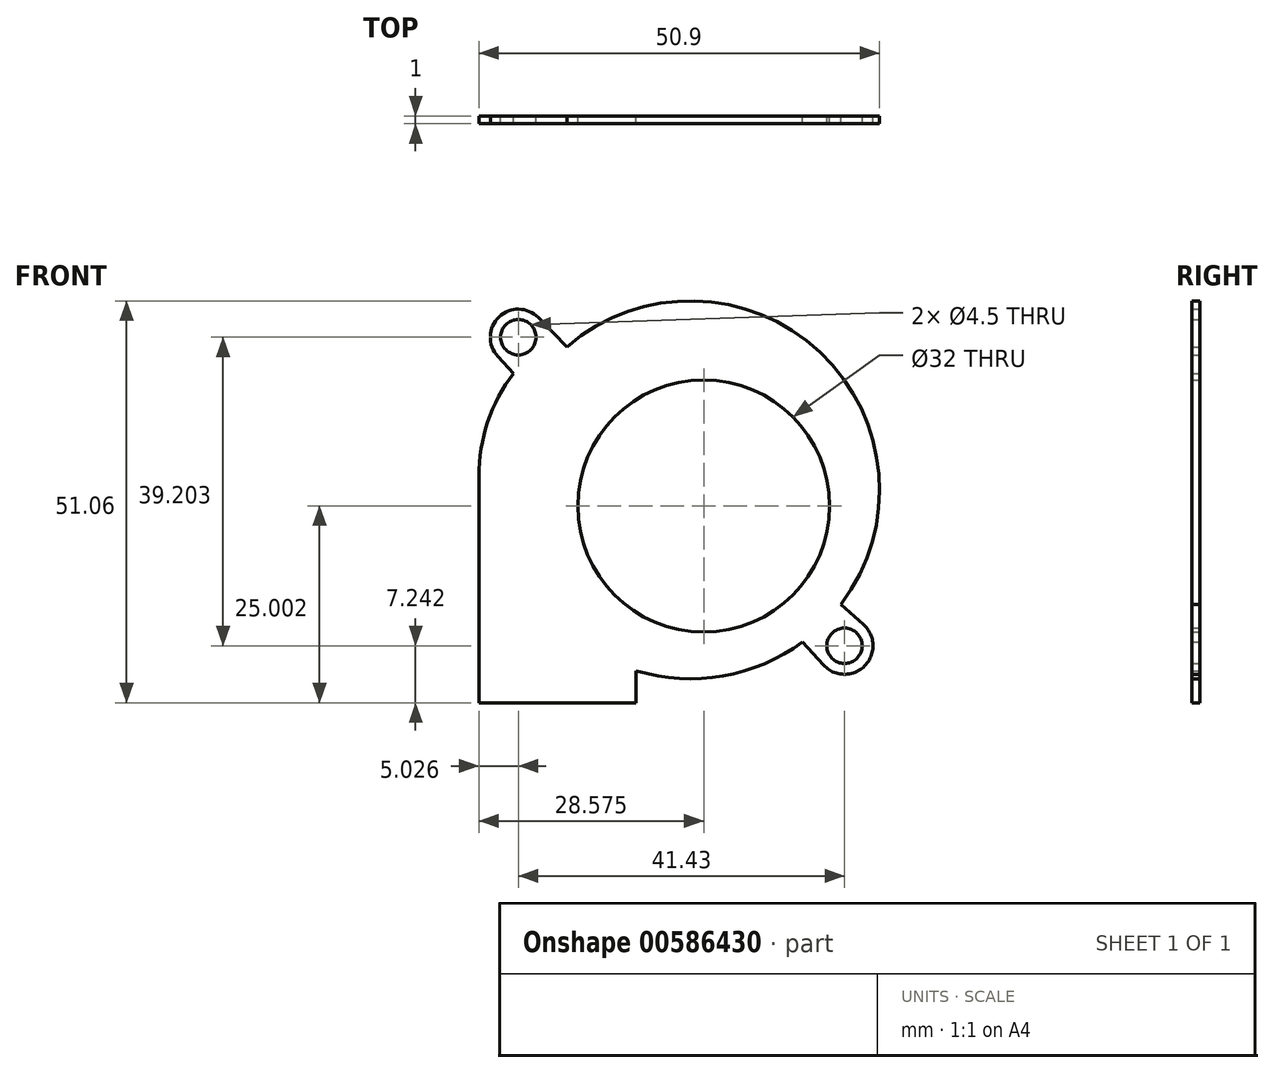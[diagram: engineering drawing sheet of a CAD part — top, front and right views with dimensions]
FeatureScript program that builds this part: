
annotation { "Feature Type Name" : "Feature", "Feature Type Description" : "" }
export const myFeature = defineFeature(function(context is Context, id is Id, definition is map)
    precondition{}
    {
        {
            var Q0;
            Q0=qCreatedBy(makeId("Front.planeOp"),FACE);
            var sketch = newSketch(context, id + "F0", { "sketchPlane" : qUnion([Q0])});
            skCircle(sketch, "E0", {"center": v(12.78, 22.35) * mm, "radius": 16 * mm});
            skPoint(sketch, "E0.first.point", {"position": v(12.7, 6.35) * mm});
            skPoint(sketch, "E0.second.point", {"position": v(-2.06, 28.32) * mm});
            skPoint(sketch, "E0.third.point", {"position": v(26, 31.38) * mm});
            skArc(sketch, "E1", {"start": v(4.2, 1.42) * mm, "mid": v(15.2, 0.76) * mm, "end": v(25.34, 5.08) * mm});
            skPoint(sketch, "E1.first.point", {"position": v(2, 46.61) * mm});
            skPoint(sketch, "E1.second.point", {"position": v(28.03, 41.43) * mm});
            skPoint(sketch, "E1.third.point", {"position": v(32.75, 14.02) * mm});
            skLineSegment(sketch, "E2", {"start": v(4.2, -2.65) * mm, "end": v(-15.8, -2.65) * mm});
            skLineSegment(sketch, "E3", {"start": v(-15.8, -2.65) * mm, "end": v(-15.8, 26.12) * mm});
            skLineSegment(sketch, "E4", {"start": v(4.2, -2.65) * mm, "end": v(4.2, 1.42) * mm});
            skCircle(sketch, "E5", {"center": v(-10.76, 43.8) * mm, "radius": 2.25 * mm});
            skCircle(sketch, "E6", {"center": v(30.67, 4.6) * mm, "radius": 2.25 * mm});
            skArc(sketch, "E7", {"start": v(-8.23, 46.29) * mm, "mid": v(-13.22, 46.36) * mm, "end": v(-13.36, 41.37) * mm});
            skArc(sketch, "E8", {"start": v(27.99, 2.16) * mm, "mid": v(33.23, 2.04) * mm, "end": v(33.09, 7.28) * mm});
            skLineSegment(sketch, "E9", {"start": v(33.09, 7.28) * mm, "end": v(30.21, 9.88) * mm});
            skLineSegment(sketch, "E10", {"start": v(27.99, 2.16) * mm, "end": v(25.34, 5.08) * mm});
            skArc(sketch, "E11.trimOffspring", {"start": v(-11.35, 39.2) * mm, "mid": v(-14.65, 33.03) * mm, "end": v(-15.8, 26.12) * mm});
            skArc(sketch, "E12.trimOffspring", {"start": v(30.21, 9.88) * mm, "mid": v(27.55, 41.9) * mm, "end": v(-4.57, 42.57) * mm});
            skLineSegment(sketch, "E13", {"start": v(-4.57, 42.57) * mm, "end": v(-8.23, 46.29) * mm});
            skLineSegment(sketch, "E14", {"start": v(-11.35, 39.2) * mm, "end": v(-13.36, 41.37) * mm});
            skSolve(sketch);
        }
        {
            var Q0;
            Q0=makeQuery(id+"F0.imprint","IMPRINT",FACE,{"disambiguationData":[TD([[makeQuery(id+"F0.imprint","IMPRINT",EDGE,{"derivedFrom":sQuery(id+"F0.wireOp",EDGE,"E0")}),-1.0]])]});
            extrude(context, id + "F1", {"entities" : qUnion([Q0]), "depth" : 1 * mm, "offsetDistance" : 25.4 * mm});
        }
    });
